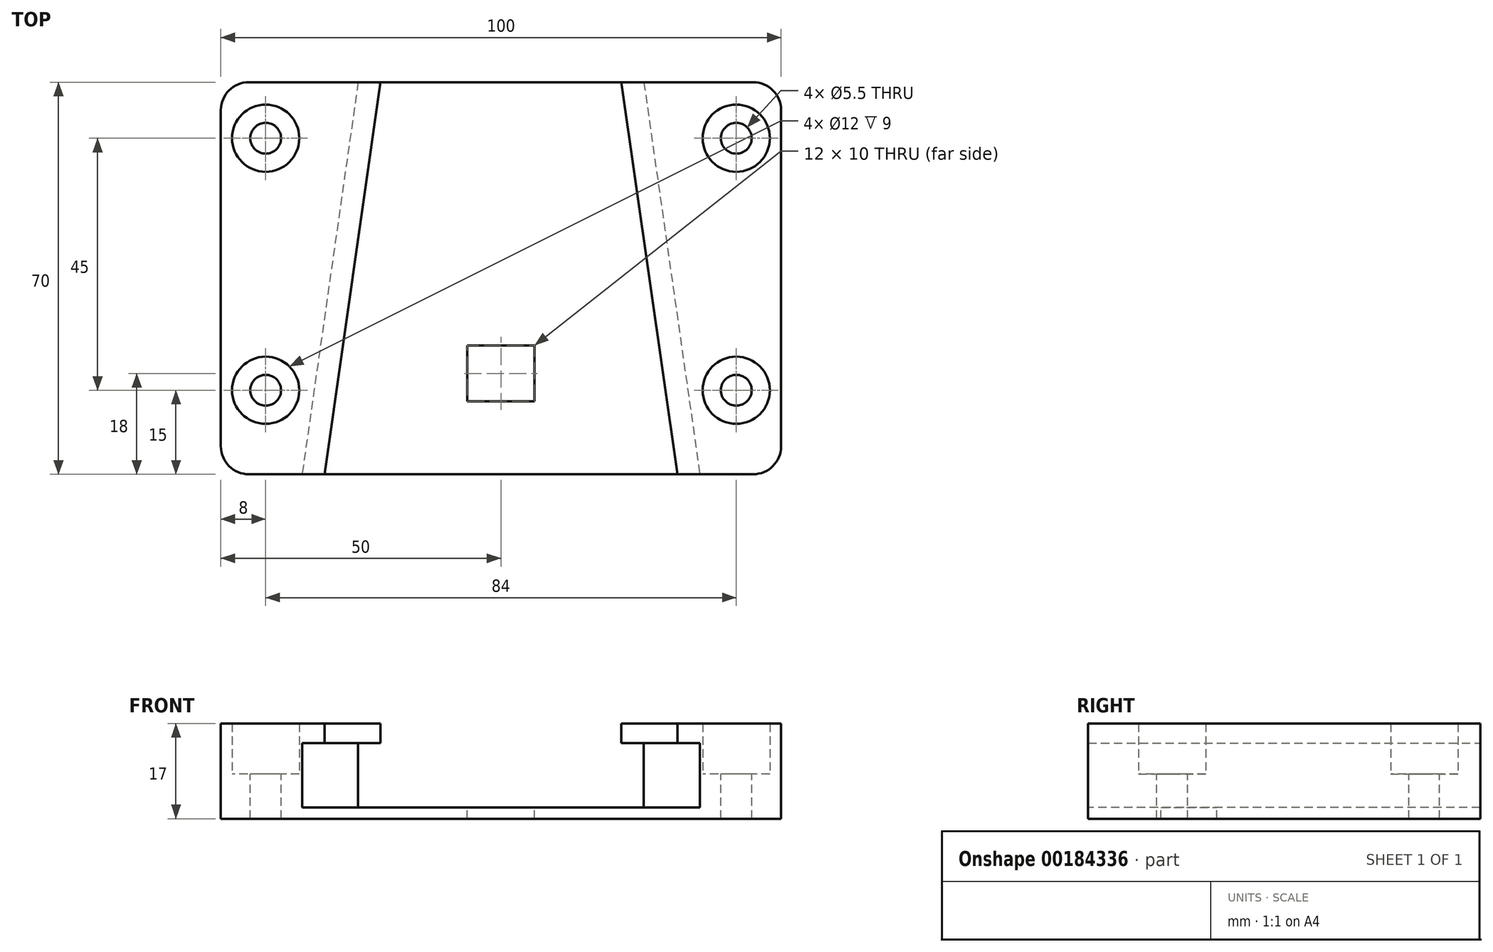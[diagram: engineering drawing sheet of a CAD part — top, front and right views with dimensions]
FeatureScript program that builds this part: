
annotation { "Feature Type Name" : "Feature", "Feature Type Description" : "" }
export const myFeature = defineFeature(function(context is Context, id is Id, definition is map)
    precondition{}
    {
        {
            var Q0;
            Q0=qCreatedBy(makeId("Top.planeOp"),FACE);
            var sketch = newSketch(context, id + "F0", { "sketchPlane" : qUnion([Q0])});
            skLineSegment(sketch, "E0.bottom", {"start": v(-45, 35) * mm, "end": v(45, 35) * mm});
            skLineSegment(sketch, "E0.top", {"start": v(-45, -35) * mm, "end": v(45, -35) * mm});
            skLineSegment(sketch, "E0.left", {"start": v(-50, 30) * mm, "end": v(-50, -30) * mm});
            skLineSegment(sketch, "E0.right", {"start": v(50, 30) * mm, "end": v(50, -30) * mm});
            skPoint(sketch, "E0.middle", {"position": v(0, 0) * mm});
            skLineSegment(sketch, "E1", {"start": v(-25.5, 35) * mm, "end": v(-35.5, -35) * mm});
            skLineSegment(sketch, "E2", {"start": v(25.5, 35) * mm, "end": v(35.5, -35) * mm});
            skLineSegment(sketch, "E3", {"start": v(-25.5, 35) * mm, "end": v(25.5, 35) * mm});
            skPoint(sketch, "E4.visualSharp", {"position": v(-50, 35) * mm});
            skArc(sketch, "E4.filletArc", {"start": v(-45, 35) * mm, "mid": v(-48.54, 33.54) * mm, "end": v(-50, 30) * mm});
            skPoint(sketch, "E5.visualSharp", {"position": v(50, 35) * mm});
            skArc(sketch, "E5.filletArc", {"start": v(50, 30) * mm, "mid": v(48.54, 33.54) * mm, "end": v(45, 35) * mm});
            skPoint(sketch, "E6.visualSharp", {"position": v(50, -35) * mm});
            skArc(sketch, "E6.filletArc", {"start": v(45, -35) * mm, "mid": v(48.54, -33.54) * mm, "end": v(50, -30) * mm});
            skPoint(sketch, "E7.visualSharp", {"position": v(-50, -35) * mm});
            skArc(sketch, "E7.filletArc", {"start": v(-50, -30) * mm, "mid": v(-48.54, -33.54) * mm, "end": v(-45, -35) * mm});
            skPoint(sketch, "E8.visualSharp", {"position": v(-25.5, 35) * mm});
            skLineSegment(sketch, "E8.filletArc", {"start": v(-25.5, 35) * mm, "end": v(-25.5, 35) * mm});
            skPoint(sketch, "E9.visualSharp", {"position": v(25.5, 35) * mm});
            skLineSegment(sketch, "E9.filletArc", {"start": v(25.5, 35) * mm, "end": v(25.5, 35) * mm});
            skLineSegment(sketch, "E10.bottom", {"start": v(6, -22) * mm, "end": v(-6, -22) * mm});
            skLineSegment(sketch, "E10.top", {"start": v(6, -12) * mm, "end": v(-6, -12) * mm});
            skLineSegment(sketch, "E10.left", {"start": v(6, -22) * mm, "end": v(6, -12) * mm});
            skLineSegment(sketch, "E10.right", {"start": v(-6, -22) * mm, "end": v(-6, -12) * mm});
            skPoint(sketch, "E10.middle", {"position": v(0, -17) * mm});
            skCircle(sketch, "E11", {"center": v(-42, -20) * mm, "radius": 2.75 * mm});
            skCircle(sketch, "E12.0.1.0", {"center": v(-42, 25) * mm, "radius": 2.75 * mm});
            skCircle(sketch, "E12.1.0.0", {"center": v(42, -20) * mm, "radius": 2.75 * mm});
            skCircle(sketch, "E12.1.1.0", {"center": v(42, 25) * mm, "radius": 2.75 * mm});
            skLineSegment(sketch, "E12.direction1", {"start": v(-42, -20) * mm, "end": v(42, -20) * mm, "construction": true});
            skLineSegment(sketch, "E12.direction2", {"start": v(-42, -20) * mm, "end": v(-42, 25) * mm, "construction": true});
            skCircle(sketch, "E13", {"center": v(-42, 25) * mm, "radius": 6 * mm});
            skCircle(sketch, "E14.0.1.0", {"center": v(-42, -20) * mm, "radius": 6 * mm});
            skCircle(sketch, "E14.1.0.0", {"center": v(42, 25) * mm, "radius": 6 * mm});
            skCircle(sketch, "E14.1.1.0", {"center": v(42, -20) * mm, "radius": 6 * mm});
            skLineSegment(sketch, "E14.direction1", {"start": v(-42, 25) * mm, "end": v(42, 25) * mm, "construction": true});
            skLineSegment(sketch, "E14.direction2", {"start": v(-42, 25) * mm, "end": v(-42, -20) * mm, "construction": true});
            skSolve(sketch);
        }
        {
            var Q0;
            Q0=makeQuery(id+"F0.imprint","IMPRINT",FACE,{"disambiguationData":[TD([[makeQuery(id+"F0.imprint","IMPRINT",EDGE,{"derivedFrom":sQuery(id+"F0.wireOp",EDGE,"E0.left")}),1.0]])]});
            var Q1;
            {var subQ0=sQuery(id+"F0.wireOp",EDGE,"E1");Q1=makeQuery(id+"F0.imprint","IMPRINT",FACE,{"disambiguationData":[TD([[makeQuery(id+"F0.imprint","IMPRINT",EDGE,{"derivedFrom":subQ0}),-1.0]])]});}
            var Q2;
            {var subQ0=sQuery(id+"F0.wireOp",EDGE,"E1");Q2=makeQuery(id+"F0.imprint","IMPRINT",FACE,{"disambiguationData":[TD([[makeQuery(id+"F0.imprint","IMPRINT",EDGE,{"derivedFrom":subQ0}),1.0]])]});}
            var Q3;
            {var subQ0=sQuery(id+"F0.wireOp",EDGE,"E2");Q3=makeQuery(id+"F0.imprint","IMPRINT",FACE,{"disambiguationData":[TD([[makeQuery(id+"F0.imprint","IMPRINT",EDGE,{"derivedFrom":subQ0}),1.0]])]});}
            var Q4;
            Q4=makeQuery(id+"F0.imprint","IMPRINT",FACE,{"disambiguationData":[TD([[makeQuery(id+"F0.imprint","IMPRINT",EDGE,{"derivedFrom":sQuery(id+"F0.wireOp",EDGE,"E0.right")}),-1.0]])]});
            var Q5;
            Q5=makeQuery(id+"F0.imprint","IMPRINT",FACE,{"disambiguationData":[TD([[makeQuery(id+"F0.imprint","IMPRINT",EDGE,{"derivedFrom":sQuery(id+"F0.wireOp",EDGE,"E12.0.1.0")}),-1.0]])]});
            var Q6;
            Q6=makeQuery(id+"F0.imprint","IMPRINT",FACE,{"disambiguationData":[TD([[makeQuery(id+"F0.imprint","IMPRINT",EDGE,{"derivedFrom":sQuery(id+"F0.wireOp",EDGE,"E11")}),-1.0]])]});
            var Q7;
            Q7=makeQuery(id+"F0.imprint","IMPRINT",FACE,{"disambiguationData":[TD([[makeQuery(id+"F0.imprint","IMPRINT",EDGE,{"derivedFrom":sQuery(id+"F0.wireOp",EDGE,"E12.1.0.0")}),-1.0]])]});
            var Q8;
            Q8=makeQuery(id+"F0.imprint","IMPRINT",FACE,{"disambiguationData":[TD([[makeQuery(id+"F0.imprint","IMPRINT",EDGE,{"derivedFrom":sQuery(id+"F0.wireOp",EDGE,"E12.1.1.0")}),-1.0]])]});
            extrude(context, id + "F1", {"entities" : qUnion([Q0, Q1, Q2, Q3, Q4, Q5, Q6, Q7, Q8]), "oppositeDirection" : true, "depth" : 2 * mm});
        }
        {
            var Q0;
            {var subQ0=sQuery(id+"F0.wireOp",EDGE,"E1");Q0=makeQuery(id+"F0.imprint","IMPRINT",FACE,{"disambiguationData":[TD([[makeQuery(id+"F0.imprint","IMPRINT",EDGE,{"derivedFrom":subQ0}),-1.0]])]});}
            var Q1;
            {var subQ0=sQuery(id+"F0.wireOp",EDGE,"E2");Q1=makeQuery(id+"F0.imprint","IMPRINT",FACE,{"disambiguationData":[TD([[makeQuery(id+"F0.imprint","IMPRINT",EDGE,{"derivedFrom":subQ0}),1.0]])]});}
            var Q2;
            Q2=makeQuery(id+"F0.imprint","IMPRINT",FACE,{"disambiguationData":[TD([[makeQuery(id+"F0.imprint","IMPRINT",EDGE,{"derivedFrom":sQuery(id+"F0.wireOp",EDGE,"E0.right")}),-1.0]])]});
            var Q3;
            Q3=makeQuery(id+"F0.imprint","IMPRINT",FACE,{"disambiguationData":[TD([[makeQuery(id+"F0.imprint","IMPRINT",EDGE,{"derivedFrom":sQuery(id+"F0.wireOp",EDGE,"E0.left")}),1.0]])]});
            extrude(context, id + "F2", {"entities" : qUnion([Q0, Q1, Q2, Q3]), "operationType" : NewBodyOperationType.ADD, "depth" : 15 * mm});
        }
        {
            var Q0;
            {var subQ0=sQuery(id+"F0.wireOp",EDGE,"E0.top");Q0=makeQuery(id+"F2.boolean.opBoolean","MERGE",FACE,{"derivedFrom":[makeQuery(id+"F1.opExtrude","SWEPT_FACE",FACE,{"disambiguationData":[OSD([subQ0])]}),makeQuery(id+"F2.opExtrude","SWEPT_FACE",FACE,{"disambiguationData":[OSD([subQ0]),TDD([makeQuery(id+"F0.imprint","IMPRINT",EDGE,{"disambiguationData":[TD([[makeQuery(id+"F0.imprint","INTERSECT",VERTEX,{"derivedFrom":[subQ0,sQuery(id+"F0.wireOp",EDGE,"E7.filletArc")]}),-1.0]])],"derivedFrom":subQ0})])]}),makeQuery(id+"F2.opExtrude","SWEPT_FACE",FACE,{"disambiguationData":[OSD([subQ0]),TDD([makeQuery(id+"F0.imprint","IMPRINT",EDGE,{"disambiguationData":[TD([[makeQuery(id+"F0.imprint","INTERSECT",VERTEX,{"derivedFrom":[subQ0,sQuery(id+"F0.wireOp",EDGE,"E6.filletArc")]}),1.0]])],"derivedFrom":subQ0})])]})]});}
            var sketch = newSketch(context, id + "F3", { "sketchPlane" : qUnion([Q0])});
            skLineSegment(sketch, "E15.bottom", {"start": v(-35.5, 15) * mm, "end": v(-31.5, 15) * mm});
            skLineSegment(sketch, "E15.top", {"start": v(-35.5, 11.5) * mm, "end": v(-31.5, 11.5) * mm});
            skLineSegment(sketch, "E15.left", {"start": v(-35.5, 15) * mm, "end": v(-35.5, 11.5) * mm});
            skLineSegment(sketch, "E15.right", {"start": v(-31.5, 15) * mm, "end": v(-31.5, 11.5) * mm});
            skLineSegment(sketch, "E16.bottom", {"start": v(35.5, 15) * mm, "end": v(31.5, 15) * mm});
            skLineSegment(sketch, "E16.top", {"start": v(35.5, 11.5) * mm, "end": v(31.5, 11.5) * mm});
            skLineSegment(sketch, "E16.left", {"start": v(35.5, 15) * mm, "end": v(35.5, 11.5) * mm});
            skLineSegment(sketch, "E16.right", {"start": v(31.5, 15) * mm, "end": v(31.5, 11.5) * mm});
            skSolve(sketch);
        }
        {
            var Q0;
            Q0=makeQuery(id+"F3.imprint","IMPRINT",FACE,{"disambiguationData":[TD([[makeQuery(id+"F3.imprint","IMPRINT",EDGE,{"derivedFrom":sQuery(id+"F3.wireOp",EDGE,"E15.bottom")}),-1.0]])]});
            var Q1;
            Q1=makeQuery(id+"F2.opExtrude","CAP_EDGE",EDGE,{"disambiguationData":[OSD([sQuery(id+"F0.wireOp",EDGE,"E1")])],"isStart":false});
            sweep(context, id + "F4", {"operationType" : NewBodyOperationType.ADD, "profiles" : qUnion([Q0]), "path" : qUnion([Q1])});
        }
        {
            var Q0;
            Q0=makeQuery(id+"F3.imprint","IMPRINT",FACE,{"disambiguationData":[TD([[makeQuery(id+"F3.imprint","IMPRINT",EDGE,{"derivedFrom":sQuery(id+"F3.wireOp",EDGE,"E16.bottom")}),1.0]])]});
            var Q1;
            Q1=makeQuery(id+"F2.opExtrude","CAP_EDGE",EDGE,{"disambiguationData":[OSD([sQuery(id+"F0.wireOp",EDGE,"E2")])],"isStart":false});
            sweep(context, id + "F5", {"operationType" : NewBodyOperationType.ADD, "profiles" : qUnion([Q0]), "path" : qUnion([Q1])});
        }
        {
            var Q0;
            Q0=makeQuery(id+"F0.imprint","IMPRINT",FACE,{"disambiguationData":[TD([[makeQuery(id+"F0.imprint","IMPRINT",EDGE,{"derivedFrom":sQuery(id+"F0.wireOp",EDGE,"E11")}),-1.0]])]});
            var Q1;
            Q1=makeQuery(id+"F0.imprint","IMPRINT",FACE,{"disambiguationData":[TD([[makeQuery(id+"F0.imprint","IMPRINT",EDGE,{"derivedFrom":sQuery(id+"F0.wireOp",EDGE,"E12.0.1.0")}),-1.0]])]});
            var Q2;
            Q2=makeQuery(id+"F0.imprint","IMPRINT",FACE,{"disambiguationData":[TD([[makeQuery(id+"F0.imprint","IMPRINT",EDGE,{"derivedFrom":sQuery(id+"F0.wireOp",EDGE,"E12.1.1.0")}),-1.0]])]});
            var Q3;
            Q3=makeQuery(id+"F0.imprint","IMPRINT",FACE,{"disambiguationData":[TD([[makeQuery(id+"F0.imprint","IMPRINT",EDGE,{"derivedFrom":sQuery(id+"F0.wireOp",EDGE,"E12.1.0.0")}),-1.0]])]});
            extrude(context, id + "F6", {"entities" : qUnion([Q0, Q1, Q2, Q3]), "operationType" : NewBodyOperationType.ADD, "depth" : 6 * mm});
        }
    });
